# Revit family: Light_Fixture-Wall_Sconce-KOHLER-Components-K-23467
name_source: partatom
category: Lighting Fixtures
revit_build: Autodesk Revit 2017 (Build: 20160225_1515(x64)
units: mm (PartAtom-declared; Revit-internal decimal feet)

## family parameters
Cut with Voids When Loaded = No
Host = Face
Light Source = Yes
OmniClass Number = 23.35.47.11
OmniClass Title = Lighting Fixtures
Part Type = Normal
Room Calculation Point = No
Round Connector Dimension = Use Diameter
Shared = No

## types (4) — shared parameters
ADA Compliant = No
Apparent Load = 10 VA
Assembly Code = D5040.50
Color Filter = 16777215
Date Modified = 05/13/2020
Default Elevation = 60"
Description = LED lacemaker sconce
Dimming Lamp Color Temperature Shift = Incandescent Lamp Curve
Electrical Connector = Yes
Electrical Note = One Circuit Required
Hardware Included = Yes
Height = 12"
Lamp = Integrated LED
Length = 7 1/4"
Light Source Symbol Size = 7"
Manufacturer = KOHLER Co.
Master Format 2014 = 26 51 13
Master Format 2014 Name = Interior Lighting Fixtures, Lamps, And Ballasts
Material = Premium Metal Construction
Product Documentation Link = https://www.us.kohler.com
Product Name = Components
Product Page URL = http://www.us.kohler.com
URL = https://www.us.kohler.com
Voltage = 120 V
WaterSense Certified = No
Wattage Comments = 10 W
Width = 6"

## per-type parameters (varying)
| type | Finish | Model | Type |
| BLL-Matte Black | KOHLER-Metal-BLL-Matte_Black | K-23467-SCLED-BLL | 1 |
| BGL-Moderne Brushed Gold | KOHLER-Metal-BGL-Moderne_Brushed_Gold | K-23467-SCLED-BGL | 2 |
| CPL-Polished Chrome | KOHLER-Metal-CPL-Polished_Chrome | K-23467-SCLED-CPL | 3 |
| SNL-Polished Nickel | KOHLER-Metal-SNL-Polished_Nickel | K-23467-SCLED-SNL | 4 |

## geometry (parser evidence)
native form markers: Sweep x6
no freeform markers — native parametric forms only
